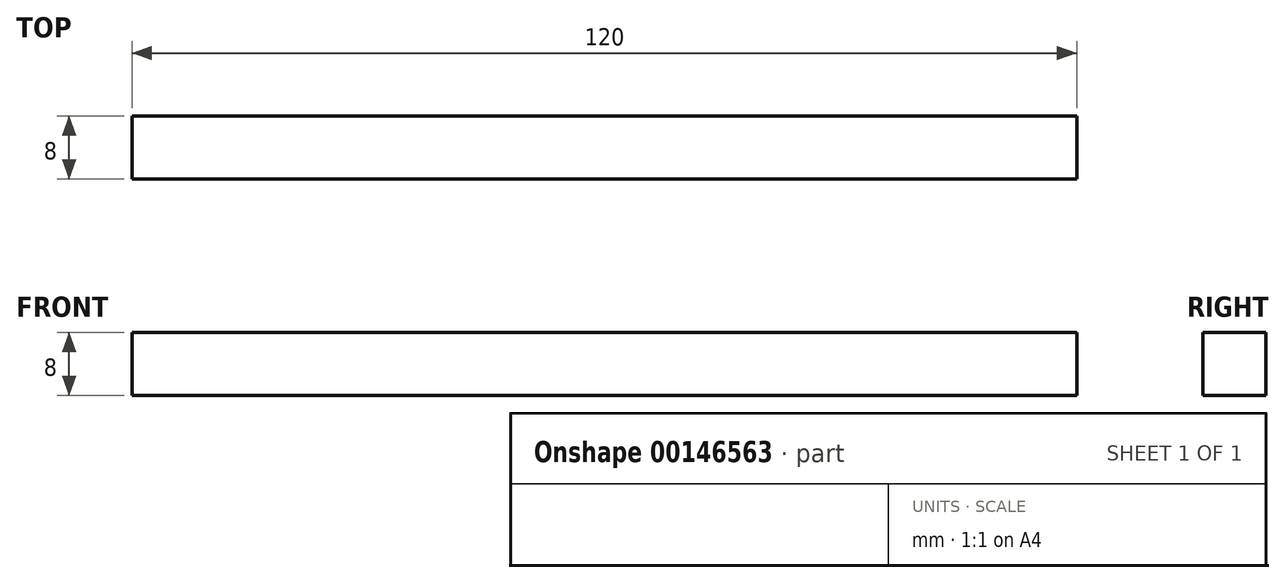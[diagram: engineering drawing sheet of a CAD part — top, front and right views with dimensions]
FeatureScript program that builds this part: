
annotation { "Feature Type Name" : "Feature", "Feature Type Description" : "" }
export const myFeature = defineFeature(function(context is Context, id is Id, definition is map)
    precondition{}
    {
        {
            assignVariable(context, id + "F0", {"name" : "width", "anyValue" : 8});
        }
        {
            var Q0;
            Q0=qCreatedBy(makeId("Front.planeOp"),FACE);
            var sketch = newSketch(context, id + "F1", { "sketchPlane" : qUnion([Q0])});
            skLineSegment(sketch, "E0", {"start": v(-60, 0) * mm, "end": v(-60, 8) * mm});
            skLineSegment(sketch, "E1", {"start": v(-60, 8) * mm, "end": v(60, 8) * mm});
            skLineSegment(sketch, "E2", {"start": v(60, 8) * mm, "end": v(60, 0) * mm});
            skLineSegment(sketch, "E3", {"start": v(60, 0) * mm, "end": v(-60, 0) * mm});
            skSolve(sketch);
        }
        {
            var Q0;
            Q0=makeQuery(id+"F1.imprint","IMPRINT",FACE,{"disambiguationData":[TD([[makeQuery(id+"F1.imprint","IMPRINT",EDGE,{"derivedFrom":sQuery(id+"F1.wireOp",EDGE,"E0")}),-1.0]])]});
            extrude(context, id + "F2", {"entities" : qUnion([Q0]), "depth" : (getVariable(context, 'width')) * mm, "symmetric" : true});
        }
    });
